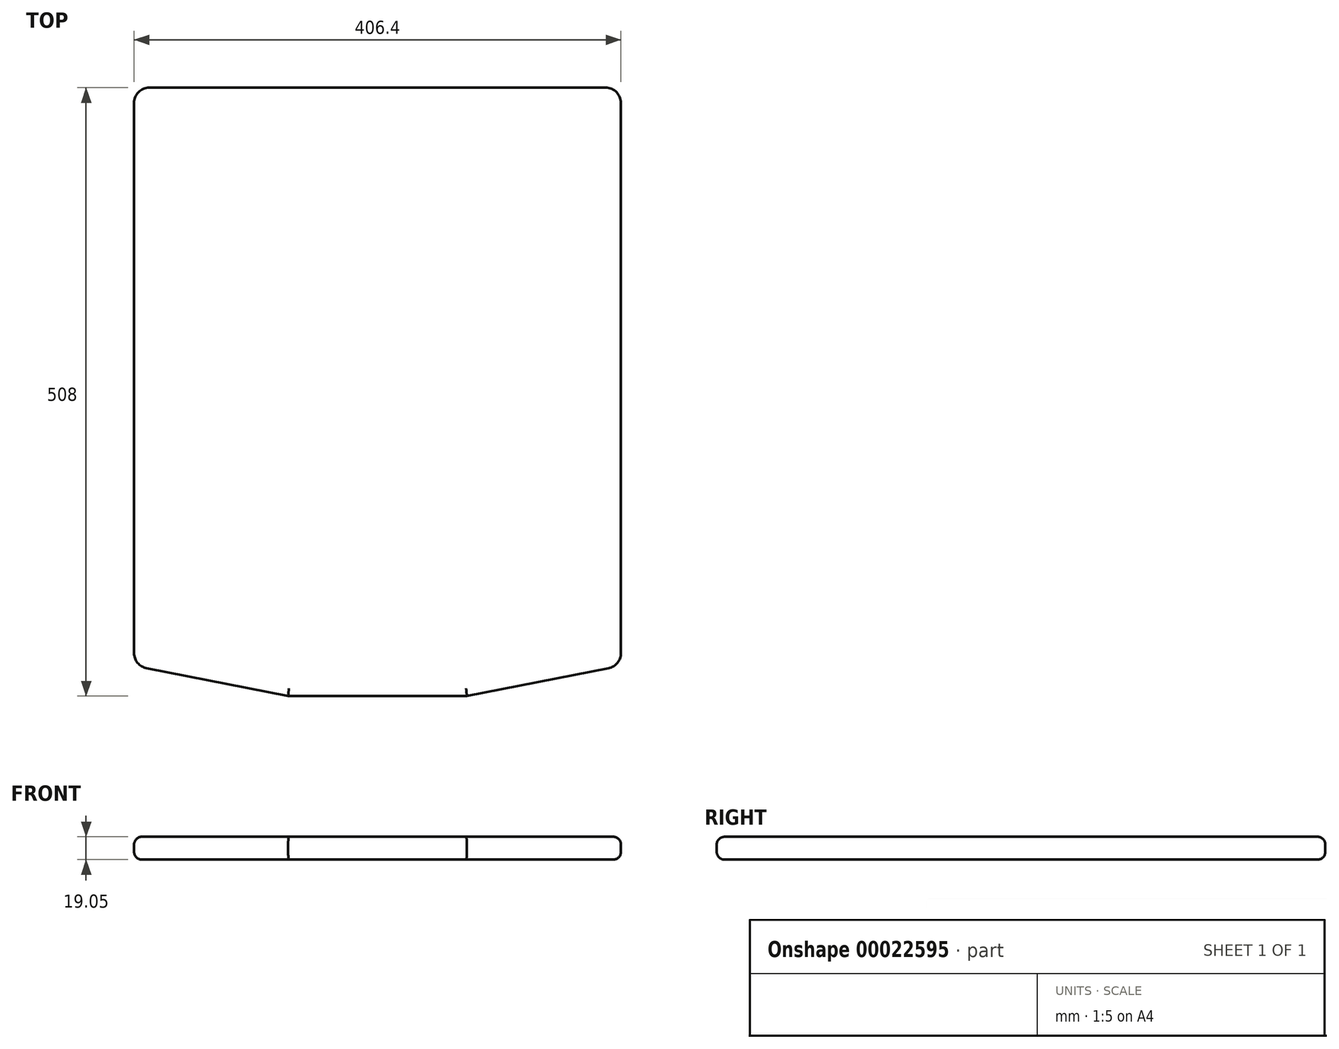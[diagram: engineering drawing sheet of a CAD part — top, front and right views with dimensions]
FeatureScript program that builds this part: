
annotation { "Feature Type Name" : "Feature", "Feature Type Description" : "" }
export const myFeature = defineFeature(function(context is Context, id is Id, definition is map)
    precondition{}
    {
        {
            var Q0;
            Q0=qCreatedBy(makeId("Top.planeOp"),FACE);
            var sketch = newSketch(context, id + "F0", { "sketchPlane" : qUnion([Q0])});
            skLineSegment(sketch, "E0.bottom", {"start": v(74.6, -254) * mm, "end": v(-74.6, -254) * mm});
            skLineSegment(sketch, "E0.top", {"start": v(190.5, 254) * mm, "end": v(-190.5, 254) * mm});
            skLineSegment(sketch, "E0.left", {"start": v(203.2, -218.16) * mm, "end": v(203.2, 241.3) * mm});
            skLineSegment(sketch, "E0.right", {"start": v(-203.2, -218.16) * mm, "end": v(-203.2, 241.3) * mm});
            skPoint(sketch, "E0.middle", {"position": v(0, 0) * mm});
            skLineSegment(sketch, "E1.top", {"start": v(74.6, 254) * mm, "end": v(-74.6, 254) * mm});
            skLineSegment(sketch, "E2", {"start": v(-192.96, -230.62) * mm, "end": v(-74.6, -254) * mm});
            skLineSegment(sketch, "E3", {"start": v(74.6, -254) * mm, "end": v(192.96, -230.62) * mm});
            skPoint(sketch, "E4.orphan", {"position": v(203.2, -254) * mm});
            skPoint(sketch, "E5.orphan", {"position": v(-203.2, -254) * mm});
            skPoint(sketch, "E6.visualSharp", {"position": v(-203.2, -228.6) * mm});
            skArc(sketch, "E6.filletArc", {"start": v(-203.2, -218.16) * mm, "mid": v(-200.31, -226.23) * mm, "end": v(-192.96, -230.62) * mm});
            skPoint(sketch, "E7.visualSharp", {"position": v(203.2, -228.6) * mm});
            skArc(sketch, "E7.filletArc", {"start": v(192.96, -230.62) * mm, "mid": v(200.31, -226.23) * mm, "end": v(203.2, -218.16) * mm});
            skPoint(sketch, "E8.visualSharp", {"position": v(203.2, 254) * mm});
            skArc(sketch, "E8.filletArc", {"start": v(203.2, 241.3) * mm, "mid": v(199.48, 250.28) * mm, "end": v(190.5, 254) * mm});
            skPoint(sketch, "E9.visualSharp", {"position": v(-203.2, 254) * mm});
            skArc(sketch, "E9.filletArc", {"start": v(-190.5, 254) * mm, "mid": v(-199.48, 250.28) * mm, "end": v(-203.2, 241.3) * mm});
            skSolve(sketch);
        }
        {
            var Q0;
            Q0=makeQuery(id+"F0.imprint","IMPRINT",FACE,{"disambiguationData":[TD([[makeQuery(id+"F0.imprint","IMPRINT",EDGE,{"derivedFrom":sQuery(id+"F0.wireOp",EDGE,"E0.bottom")}),-1.0]])]});
            extrude(context, id + "F1", {"entities" : qUnion([Q0]), "depth" : 19.05 * mm, "offsetDistance" : 25.4 * mm});
        }
        {
            var Q0;
            Q0=makeQuery(id+"F1.opExtrude","CAP_FACE",FACE,{"disambiguationData":[OSD([sQuery(id+"F0.wireOp",EDGE,"E0.bottom"),sQuery(id+"F0.wireOp",EDGE,"E0.top"),sQuery(id+"F0.wireOp",EDGE,"E0.left"),sQuery(id+"F0.wireOp",EDGE,"E0.right"),sQuery(id+"F0.wireOp",EDGE,"E2"),sQuery(id+"F0.wireOp",EDGE,"E3"),sQuery(id+"F0.wireOp",EDGE,"E6.filletArc"),sQuery(id+"F0.wireOp",EDGE,"E7.filletArc"),sQuery(id+"F0.wireOp",EDGE,"E8.filletArc"),sQuery(id+"F0.wireOp",EDGE,"E9.filletArc")])],"isStart":false});
            fillet(context, id + "F2", {"entities" : qUnion([Q0]), "tangentPropagation" : true, "radius" : 6.35 * mm, "defaultsChanged" : true, "vertexSettings" : [], "allowEdgeOverflow" : false});
        }
        {
            var Q0;
            Q0=makeQuery(id+"F1.opExtrude","CAP_FACE",FACE,{"disambiguationData":[OSD([sQuery(id+"F0.wireOp",EDGE,"E0.bottom"),sQuery(id+"F0.wireOp",EDGE,"E0.top"),sQuery(id+"F0.wireOp",EDGE,"E0.left"),sQuery(id+"F0.wireOp",EDGE,"E0.right"),sQuery(id+"F0.wireOp",EDGE,"E2"),sQuery(id+"F0.wireOp",EDGE,"E3"),sQuery(id+"F0.wireOp",EDGE,"E6.filletArc"),sQuery(id+"F0.wireOp",EDGE,"E7.filletArc"),sQuery(id+"F0.wireOp",EDGE,"E8.filletArc"),sQuery(id+"F0.wireOp",EDGE,"E9.filletArc")])],"isStart":true});
            fillet(context, id + "F3", {"entities" : qUnion([Q0]), "tangentPropagation" : true, "radius" : 6.35 * mm, "defaultsChanged" : true, "vertexSettings" : [], "allowEdgeOverflow" : false});
        }
    });
